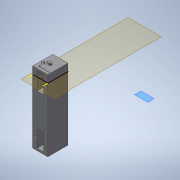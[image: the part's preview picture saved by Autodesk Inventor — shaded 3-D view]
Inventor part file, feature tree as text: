
AUTODESK INVENTOR PART (.ipt)
format: ipt  version: 2020 (Build 240168000, 168)  size: 238,080 bytes
history: native  units: mm
features: extrude x9, sketch x9, reference x8, other x6, projected_geometry x3, hole x1, mirror x1
ambient origin geometry x8: Origin, YZ Plane, XZ Plane, XY Plane, X Axis, Y Axis, Z Axis, Center Point
bodies: Body1 (feature_tree)
feature tree (37):
  other  "Bryła1"
  other  "Płaszczyzna konstrukcyjna1"
  extrude  "Wyciągnięcie proste1"  Depth=3.0mm TaperAngle=0.0deg
  extrude  "Wyciągnięcie proste2"  Depth=6.0mm
  extrude  "Wyciągnięcie proste3"  Depth=20.0mm TaperAngle=0.0deg
  sketch  "Szkic4"
  extrude  "Wyciągnięcie proste4"  Depth=0.25mm
  extrude  "Wyciągnięcie proste5"  Depth=0.25mm
  hole  "Otwór3"  [1 undecoded]
  extrude  "Wyciągnięcie proste6"  Depth=0.25mm
  extrude  "Wyciągnięcie proste7"  TaperAngle=0.0deg  [1 undecoded]
  mirror  "Odbij1"
  extrude  "Wyciągnięcie proste8"  Depth=14.6mm
  extrude  "Wyciągnięcie proste9"  TaperAngle=0.0deg  [1 undecoded]
  sketch  "Szkic1"
  reference  "Odniesienie1"
  reference  "Odniesienie2"
  sketch  "Szkic2"
  sketch  "Szkic3"
  reference  "Odniesienie3"
  reference  "Odniesienie4"
  reference  "Odniesienie5"
  reference  "Odniesienie6"
  reference  "Odniesienie7"
  sketch  "Szkic6"
  projected_geometry  "Pętla rzutowana1"
  sketch  "Szkic7"
  reference  "Odniesienie8"
  sketch  "Szkic8"
  projected_geometry  "Pętla rzutowana2"
  sketch  "Szkic9"
  projected_geometry  "Pętla rzutowana3"
  sketch  "Szkic11"
  other  "<userpath>\Desktop\3d\scanning-robot\Assembly1.iam"
  other  "Assembly1.iam"
  other  "wheel-adapter:1"
  other  "wheel-adapter-front_MIR:1"
note: 3 required parameter values undecoded (feature->parameter linkage not recoverable at this tier; creation-order binding heuristic only, values carry confidence <= 0.55)
